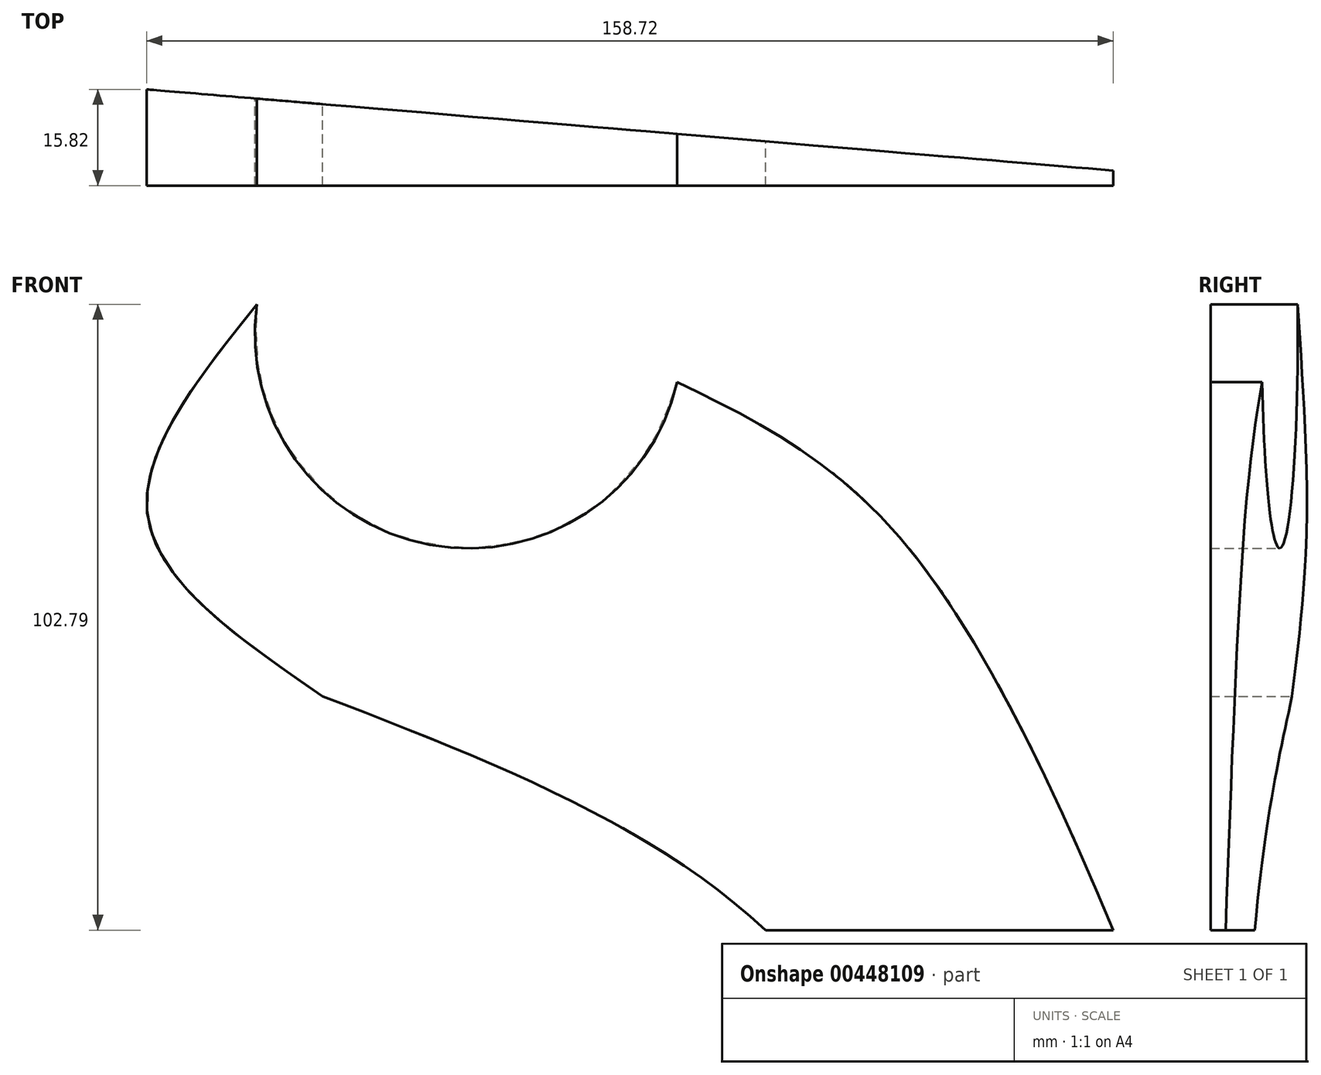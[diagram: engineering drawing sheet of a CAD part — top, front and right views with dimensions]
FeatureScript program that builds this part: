
annotation { "Feature Type Name" : "Feature", "Feature Type Description" : "" }
export const myFeature = defineFeature(function(context is Context, id is Id, definition is map)
    precondition{}
    {
        {
            var Q0;
            Q0=qCreatedBy(makeId("Front.planeOp"),FACE);
            var sketch = newSketch(context, id + "F0", { "sketchPlane" : qUnion([Q0])});
            skCircle(sketch, "E0", {"center": v(-26.7, 97.83) * mm, "radius": 35.12 * mm});
            skFitSpline(sketch, "E1", {"points": [v(62.1, -64.2) * mm, v(22.07, 0) * mm, v(-50.68, 38.4) * mm], "startDerivative": vector(-66.89, 144.85) * mm, "endDerivative": vector(-158.03, 60.97) * mm});
            skFitSpline(sketch, "E2", {"points": [v(96.41, -43.68) * mm, v(44.6, 63.9) * mm, v(7.54, 90.01) * mm], "startDerivative": vector(-79.6, 206.48) * mm, "endDerivative": vector(-99.82, 48.43) * mm});
            skFitSpline(sketch, "E3", {"points": [v(-50.68, 38.4) * mm, v(-79.41, 67.84) * mm, v(-61.48, 102.8) * mm], "startDerivative": vector(-80.38, 55.04) * mm, "endDerivative": vector(59.38, 73.8) * mm});
            skLineSegment(sketch, "E4", {"start": v(62.1, -64.2) * mm, "end": v(96.41, -43.68) * mm});
            skSolve(sketch);
        }
        {
            var Q0;
            Q0=qCreatedBy(makeId("Top.planeOp"),FACE);
            var sketch = newSketch(context, id + "F1", { "sketchPlane" : qUnion([Q0])});
            skLineSegment(sketch, "E5.bottom", {"start": v(-108.67, 25.73) * mm, "end": v(108.67, 25.73) * mm});
            skLineSegment(sketch, "E5.top", {"start": v(-108.67, -25.73) * mm, "end": v(108.67, -25.73) * mm});
            skLineSegment(sketch, "E5.left", {"start": v(-108.67, 25.73) * mm, "end": v(-108.67, -25.73) * mm});
            skLineSegment(sketch, "E5.right", {"start": v(108.67, 25.73) * mm, "end": v(108.67, -25.73) * mm});
            skPoint(sketch, "E5.middle", {"position": v(0, 0) * mm});
            skLineSegment(sketch, "E6", {"start": v(108.67, -25.73) * mm, "end": v(-108.67, -7.47) * mm});
            skSolve(sketch);
        }
        {
            var Q0;
            Q0=makeQuery(id+"F0.imprint","IMPRINT",FACE,{"disambiguationData":[TD([[makeQuery(id+"F0.imprint","IMPRINT",EDGE,{"derivedFrom":sQuery(id+"F0.wireOp",EDGE,"E1")}),-1.0]])]});
            var Q1;
            Q1=sQuery(id+"F1.wireOp",VERTEX,"E6.start");
            extrude(context, id + "F2", {"entities" : qUnion([Q0]), "endBound" : BoundingType.UP_TO_VERTEX, "endBoundEntityVertex" : qUnion([Q1]), "depth" : 25 * mm});
        }
        {
            var Q0;
            Q0 = qSketchRegion(id + "F0ZMnSsRMHEzuU2_1", true);
            var Q1;
            {var subQ0=sQuery(id+"F1.wireOp",EDGE,"E5.top");Q1=makeQuery(id+"F1.imprint","IMPRINT",FACE,{"disambiguationData":[TD([[makeQuery(id+"F1.imprint","IMPRINT",EDGE,{"derivedFrom":subQ0}),1.0]])]});}
            extrude(context, id + "F3", {"entities" : qUnion([Q0, Q1]), "endBound" : BoundingType.THROUGH_ALL, "depth" : 25 * mm});
        }
        {
            var Q0;
            Q0=makeQuery(id+"F3.opExtrude","SWEPT_BODY",BODY,{"disambiguationData":[OSD([sQuery(id+"F1.wireOp",EDGE,"E5.top"),sQuery(id+"F1.wireOp",EDGE,"E5.left"),sQuery(id+"F1.wireOp",EDGE,"E6")])]});
            var Q1;
            Q1=makeQuery(id+"F2.opExtrude","SWEPT_BODY",BODY,{"disambiguationData":[OSD([sQuery(id+"F0.wireOp",EDGE,"E0"),sQuery(id+"F0.wireOp",EDGE,"E1"),sQuery(id+"F0.wireOp",EDGE,"E2"),sQuery(id+"F0.wireOp",EDGE,"E3"),sQuery(id+"F0.wireOp",EDGE,"E4")])]});
            booleanBodies(context, id + "F4", {"operationType" : BooleanOperationType.INTERSECTION, "tools" : qUnion([Q0, Q1])});
        }
    });
